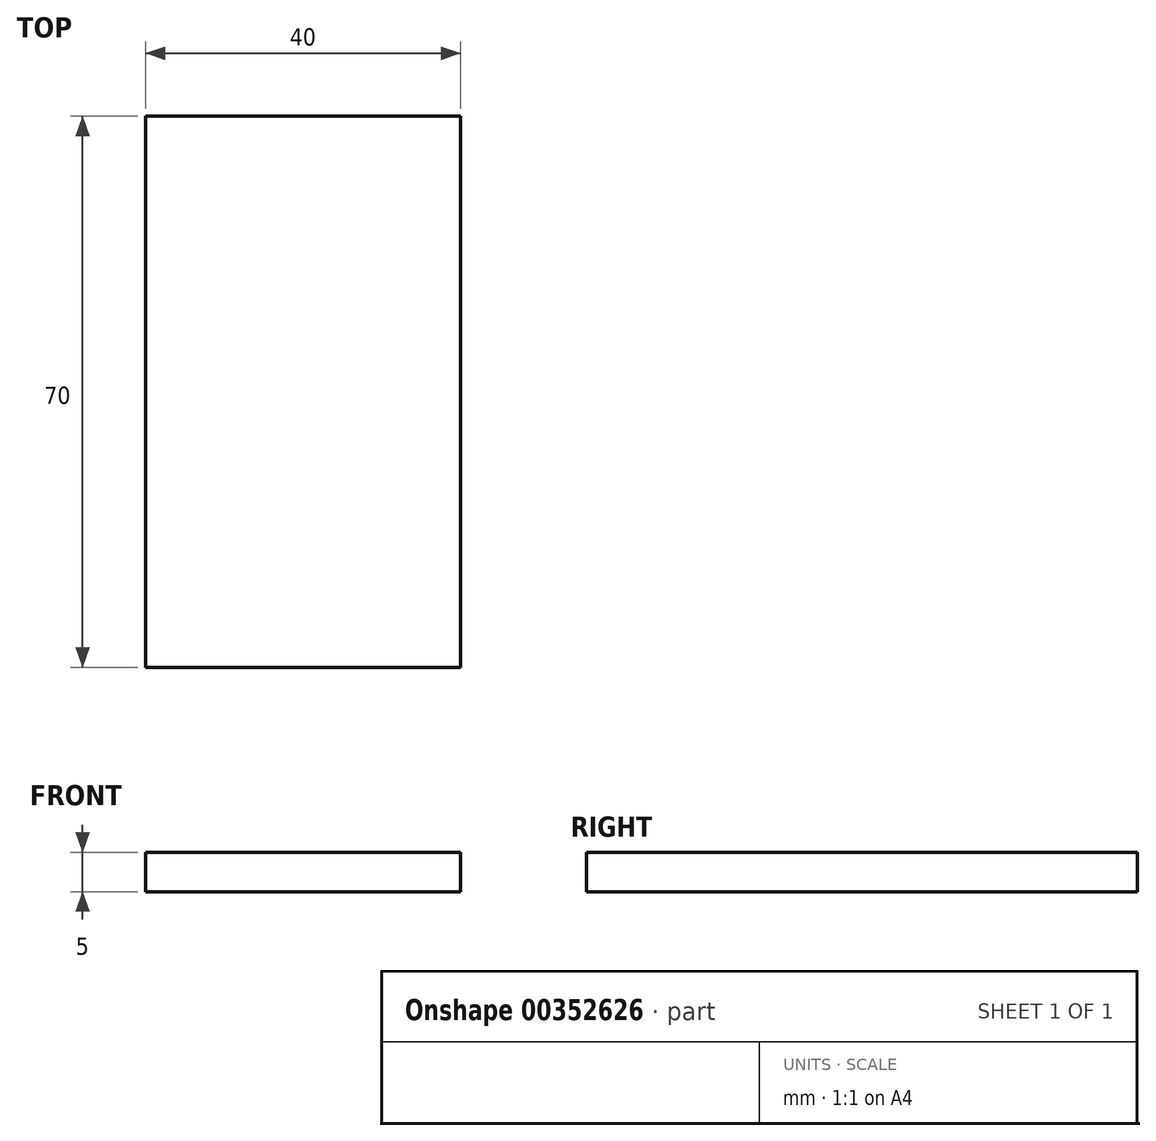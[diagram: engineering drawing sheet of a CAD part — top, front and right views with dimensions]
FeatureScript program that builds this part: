
annotation { "Feature Type Name" : "Feature", "Feature Type Description" : "" }
export const myFeature = defineFeature(function(context is Context, id is Id, definition is map)
    precondition{}
    {
        {
            var Q0;
            Q0=qCreatedBy(makeId("Top.planeOp"),FACE);
            var sketch = newSketch(context, id + "F0", { "sketchPlane" : qUnion([Q0])});
            skLineSegment(sketch, "E0.bottom", {"start": v(-20, 35) * mm, "end": v(20, 35) * mm});
            skLineSegment(sketch, "E0.top", {"start": v(-20, -35) * mm, "end": v(20, -35) * mm});
            skLineSegment(sketch, "E0.left", {"start": v(-20, 35) * mm, "end": v(-20, -35) * mm});
            skLineSegment(sketch, "E0.right", {"start": v(20, 35) * mm, "end": v(20, -35) * mm});
            skPoint(sketch, "E0.middle", {"position": v(0, 0) * mm});
            skSolve(sketch);
        }
        {
            var Q0;
            Q0 = qSketchRegion(id + "F0", true);
            extrude(context, id + "F1", {"entities" : qUnion([Q0]), "depth" : 5 * mm});
        }
    });
